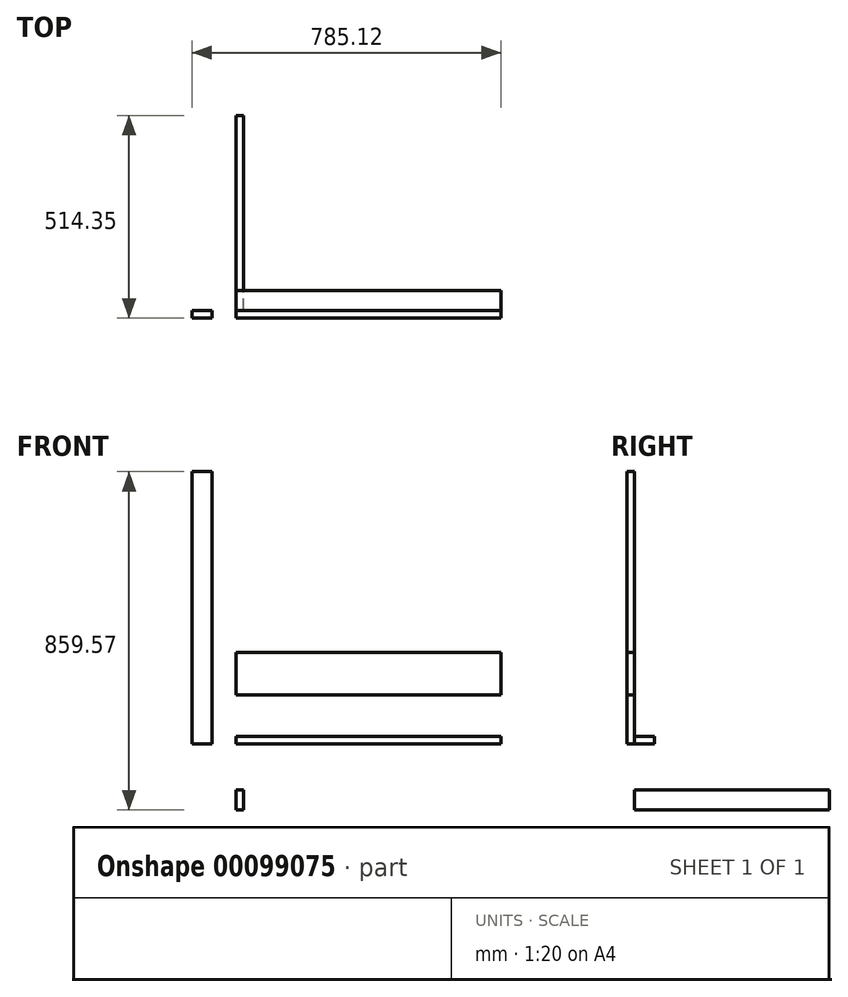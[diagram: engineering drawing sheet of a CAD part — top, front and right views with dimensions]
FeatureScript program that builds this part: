
annotation { "Feature Type Name" : "Feature", "Feature Type Description" : "" }
export const myFeature = defineFeature(function(context is Context, id is Id, definition is map)
    precondition{}
    {
        {
            var Q0;
            Q0=qCreatedBy(makeId("Top.planeOp"),FACE);
            var sketch = newSketch(context, id + "F0", { "sketchPlane" : qUnion([Q0])});
            skLineSegment(sketch, "E0.bottom", {"start": v(0, 0) * mm, "end": v(673.1, 0) * mm});
            skLineSegment(sketch, "E0.top", {"start": v(0, 50.8) * mm, "end": v(673.1, 50.8) * mm});
            skLineSegment(sketch, "E0.left", {"start": v(0, 0) * mm, "end": v(0, 50.8) * mm});
            skLineSegment(sketch, "E0.right", {"start": v(673.1, 0) * mm, "end": v(673.1, 50.8) * mm});
            skSolve(sketch);
        }
        {
            var Q0;
            Q0 = qSketchRegion(id + "F0", true);
            extrude(context, id + "F1", {"entities" : qUnion([Q0]), "depth" : 19.05 * mm});
        }
        {
            var Q0;
            Q0=qCreatedBy(makeId("Right.planeOp"),FACE);
            var sketch = newSketch(context, id + "F2", { "sketchPlane" : qUnion([Q0])});
            skLineSegment(sketch, "E1.bottom", {"start": v(0, -116.62) * mm, "end": v(495.3, -116.62) * mm});
            skLineSegment(sketch, "E1.top", {"start": v(0, -167.42) * mm, "end": v(495.3, -167.42) * mm});
            skLineSegment(sketch, "E1.left", {"start": v(0, -116.62) * mm, "end": v(0, -167.42) * mm});
            skLineSegment(sketch, "E1.right", {"start": v(495.3, -116.62) * mm, "end": v(495.3, -167.42) * mm});
            skSolve(sketch);
        }
        {
            var Q0;
            Q0 = qSketchRegion(id + "F2", true);
            extrude(context, id + "F3", {"entities" : qUnion([Q0]), "depth" : 19.05 * mm});
        }
        {
            var Q0;
            Q0=qCreatedBy(makeId("Front.planeOp"),FACE);
            var sketch = newSketch(context, id + "F4", { "sketchPlane" : qUnion([Q0])});
            skLineSegment(sketch, "E2.bottom", {"start": v(-61.22, 0) * mm, "end": v(-112.02, 0) * mm});
            skLineSegment(sketch, "E2.top", {"start": v(-61.22, 692.15) * mm, "end": v(-112.02, 692.15) * mm});
            skLineSegment(sketch, "E2.left", {"start": v(-61.22, 0) * mm, "end": v(-61.22, 692.15) * mm});
            skLineSegment(sketch, "E2.right", {"start": v(-112.02, 0) * mm, "end": v(-112.02, 692.15) * mm});
            skSolve(sketch);
        }
        {
            var Q0;
            Q0 = qSketchRegion(id + "F4", true);
            extrude(context, id + "F5", {"entities" : qUnion([Q0]), "depth" : 19.05 * mm});
        }
        {
            var Q0;
            Q0=qCreatedBy(makeId("Front.planeOp"),FACE);
            var sketch = newSketch(context, id + "F6", { "sketchPlane" : qUnion([Q0])});
            skLineSegment(sketch, "E3.bottom", {"start": v(0, 233.05) * mm, "end": v(673.1, 233.05) * mm});
            skLineSegment(sketch, "E3.top", {"start": v(0, 125.1) * mm, "end": v(673.1, 125.1) * mm});
            skLineSegment(sketch, "E3.left", {"start": v(0, 233.05) * mm, "end": v(0, 125.1) * mm});
            skLineSegment(sketch, "E3.right", {"start": v(673.1, 233.05) * mm, "end": v(673.1, 125.1) * mm});
            skSolve(sketch);
        }
        {
            var Q0;
            Q0 = qSketchRegion(id + "F6", true);
            extrude(context, id + "F7", {"entities" : qUnion([Q0]), "depth" : 19.05 * mm});
        }
    });
